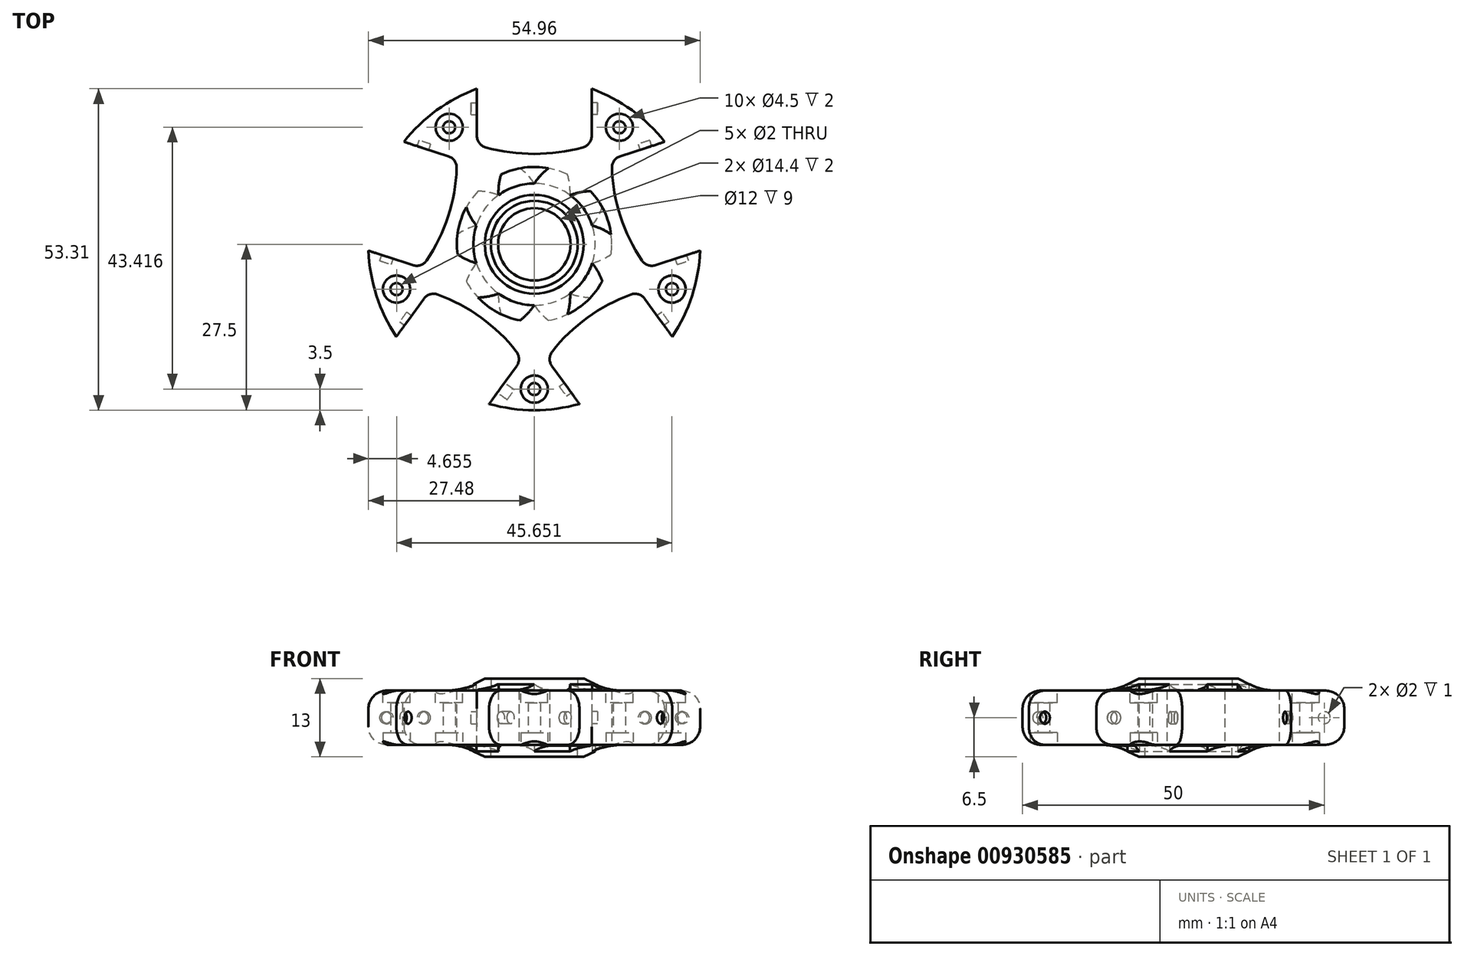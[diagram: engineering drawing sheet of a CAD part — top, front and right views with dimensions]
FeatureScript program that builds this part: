
annotation { "Feature Type Name" : "Feature", "Feature Type Description" : "" }
export const myFeature = defineFeature(function(context is Context, id is Id, definition is map)
    precondition{}
    {
        {
            var Q0;
            Q0=qCreatedBy(makeId("Top.planeOp"),FACE);
            var sketch = newSketch(context, id + "F0", { "sketchPlane" : qUnion([Q0])});
            skCircle(sketch, "E0", {"center": v(0, 0) * mm, "radius": 6 * mm});
            skArc(sketch, "E1", {"start": v(-9.5, 25.8) * mm, "mid": v(-16.16, 22.25) * mm, "end": v(-21.6, 17) * mm});
            skLineSegment(sketch, "E2", {"start": v(0, 0) * mm, "end": v(0, 27.5) * mm, "construction": true});
            skLineSegment(sketch, "E3", {"start": v(0, 0) * mm, "end": v(-26.15, 8.5) * mm, "construction": true});
            skLineSegment(sketch, "E4", {"start": v(0, 0) * mm, "end": v(26.15, 8.5) * mm, "construction": true});
            skLineSegment(sketch, "E5", {"start": v(0, 0) * mm, "end": v(-16.16, -22.25) * mm, "construction": true});
            skLineSegment(sketch, "E6", {"start": v(0, 0) * mm, "end": v(16.16, -22.25) * mm, "construction": true});
            skCircle(sketch, "E7", {"center": v(0, 0) * mm, "radius": 29 * mm, "construction": true});
            skLineSegment(sketch, "E8", {"start": v(-9.5, 25.8) * mm, "end": v(-9.5, 16.51) * mm});
            skLineSegment(sketch, "E9", {"start": v(9.5, 25.8) * mm, "end": v(9.5, 16.51) * mm});
            skCircle(sketch, "E10", {"center": v(0, 0) * mm, "radius": 24 * mm, "construction": true});
            skArc(sketch, "E11", {"start": v(-9.25, 17.51) * mm, "mid": v(0, 16) * mm, "end": v(9.25, 17.51) * mm, "construction": true});
            skLineSegment(sketch, "E12", {"start": v(9.25, 17.51) * mm, "end": v(9.25, 27.49) * mm, "construction": true});
            skLineSegment(sketch, "E13", {"start": v(-9.25, 17.51) * mm, "end": v(-9.25, 27.49) * mm, "construction": true});
            skArc(sketch, "E14", {"start": v(-9.5, 16.51) * mm, "mid": v(0, 15) * mm, "end": v(9.5, 16.51) * mm});
            skLineSegment(sketch, "E15", {"start": v(-21.6, 17) * mm, "end": v(-12.85, 14.16) * mm});
            skLineSegment(sketch, "E16", {"start": v(-27.48, -1.06) * mm, "end": v(-18.72, -3.9) * mm});
            skArc(sketch, "E17", {"start": v(-18.72, -3.9) * mm, "mid": v(-14.27, 4.64) * mm, "end": v(-12.85, 14.16) * mm});
            skArc(sketch, "E18.trimOffspring", {"start": v(-27.48, -1.06) * mm, "mid": v(-26.15, -8.5) * mm, "end": v(-22.85, -15.3) * mm});
            skLineSegment(sketch, "E19", {"start": v(-22.85, -15.3) * mm, "end": v(-17.44, -7.85) * mm});
            skLineSegment(sketch, "E20", {"start": v(-7.48, -26.46) * mm, "end": v(-2.07, -19.01) * mm});
            skArc(sketch, "E21", {"start": v(-2.07, -19.01) * mm, "mid": v(-8.82, -12.14) * mm, "end": v(-17.44, -7.85) * mm});
            skArc(sketch, "E22.trimOffspring", {"start": v(-7.48, -26.46) * mm, "mid": v(0, -27.5) * mm, "end": v(7.48, -26.46) * mm});
            skLineSegment(sketch, "E23", {"start": v(7.48, -26.46) * mm, "end": v(2.07, -19.01) * mm});
            skLineSegment(sketch, "E24", {"start": v(22.85, -15.3) * mm, "end": v(17.44, -7.85) * mm});
            skArc(sketch, "E25", {"start": v(17.44, -7.85) * mm, "mid": v(8.82, -12.14) * mm, "end": v(2.07, -19.01) * mm});
            skArc(sketch, "E26.trimOffspring", {"start": v(22.85, -15.3) * mm, "mid": v(26.15, -8.5) * mm, "end": v(27.48, -1.06) * mm});
            skLineSegment(sketch, "E27", {"start": v(21.6, 17) * mm, "end": v(12.85, 14.16) * mm});
            skLineSegment(sketch, "E28", {"start": v(27.48, -1.06) * mm, "end": v(18.72, -3.9) * mm});
            skArc(sketch, "E29", {"start": v(12.85, 14.16) * mm, "mid": v(14.27, 4.64) * mm, "end": v(18.72, -3.9) * mm});
            skArc(sketch, "E30.trimOffspring", {"start": v(21.6, 17) * mm, "mid": v(16.16, 22.25) * mm, "end": v(9.5, 25.8) * mm});
            skCircle(sketch, "E31", {"center": v(-14.1, 19.42) * mm, "radius": 1 * mm});
            skLineSegment(sketch, "E32", {"start": v(0, 0) * mm, "end": v(-14.1, 19.42) * mm, "construction": true});
            skLineSegment(sketch, "E33", {"start": v(0, 0) * mm, "end": v(14.1, 19.42) * mm, "construction": true});
            skCircle(sketch, "E34", {"center": v(14.1, 19.42) * mm, "radius": 1 * mm});
            skLineSegment(sketch, "E35", {"start": v(-22.83, -7.42) * mm, "end": v(0, 0) * mm, "construction": true});
            skLineSegment(sketch, "E36", {"start": v(0, -24) * mm, "end": v(0, 0) * mm, "construction": true});
            skLineSegment(sketch, "E37", {"start": v(0, 0) * mm, "end": v(22.83, -7.42) * mm, "construction": true});
            skCircle(sketch, "E38", {"center": v(-22.83, -7.42) * mm, "radius": 1 * mm});
            skCircle(sketch, "E39", {"center": v(0, -24) * mm, "radius": 1 * mm});
            skCircle(sketch, "E40", {"center": v(22.83, -7.42) * mm, "radius": 1 * mm});
            skLineSegment(sketch, "E41", {"start": v(-9.5, 22.5) * mm, "end": v(9.5, 22.5) * mm, "construction": true});
            skSolve(sketch);
        }
        {
            var Q0;
            Q0=qSketchRegion(id+"F0",true);
            extrude(context, id + "F1", {"entities" : qUnion([Q0]), "depth" : 9 * mm});
        }
        {
            var Q0;
            Q0=makeQuery(id+"F1.opExtrude","SWEPT_EDGE",EDGE,{"disambiguationData":[OSD([sQuery(id+"F0.wireOp",EDGE,"E8"),sQuery(id+"F0.wireOp",EDGE,"E14")])]});
            var Q1;
            Q1=makeQuery(id+"F1.opExtrude","SWEPT_EDGE",EDGE,{"disambiguationData":[OSD([sQuery(id+"F0.wireOp",EDGE,"E9"),sQuery(id+"F0.wireOp",EDGE,"E14")])]});
            var Q2;
            Q2=makeQuery(id+"F1.opExtrude","SWEPT_EDGE",EDGE,{"disambiguationData":[OSD([sQuery(id+"F0.wireOp",EDGE,"E27"),sQuery(id+"F0.wireOp",EDGE,"E29")])]});
            var Q3;
            Q3=makeQuery(id+"F1.opExtrude","SWEPT_EDGE",EDGE,{"disambiguationData":[OSD([sQuery(id+"F0.wireOp",EDGE,"E28"),sQuery(id+"F0.wireOp",EDGE,"E29")])]});
            var Q4;
            Q4=makeQuery(id+"F1.opExtrude","SWEPT_EDGE",EDGE,{"disambiguationData":[OSD([sQuery(id+"F0.wireOp",EDGE,"E24"),sQuery(id+"F0.wireOp",EDGE,"E25")])]});
            var Q5;
            Q5=makeQuery(id+"F1.opExtrude","SWEPT_EDGE",EDGE,{"disambiguationData":[OSD([sQuery(id+"F0.wireOp",EDGE,"E23"),sQuery(id+"F0.wireOp",EDGE,"E25")])]});
            var Q6;
            Q6=makeQuery(id+"F1.opExtrude","SWEPT_EDGE",EDGE,{"disambiguationData":[OSD([sQuery(id+"F0.wireOp",EDGE,"E20"),sQuery(id+"F0.wireOp",EDGE,"E21")])]});
            var Q7;
            Q7=makeQuery(id+"F1.opExtrude","SWEPT_EDGE",EDGE,{"disambiguationData":[OSD([sQuery(id+"F0.wireOp",EDGE,"E19"),sQuery(id+"F0.wireOp",EDGE,"E21")])]});
            var Q8;
            Q8=makeQuery(id+"F1.opExtrude","SWEPT_EDGE",EDGE,{"disambiguationData":[OSD([sQuery(id+"F0.wireOp",EDGE,"E16"),sQuery(id+"F0.wireOp",EDGE,"E17")])]});
            var Q9;
            Q9=makeQuery(id+"F1.opExtrude","SWEPT_EDGE",EDGE,{"disambiguationData":[OSD([sQuery(id+"F0.wireOp",EDGE,"E15"),sQuery(id+"F0.wireOp",EDGE,"E17")])]});
            fillet(context, id + "F2", {"entities" : qUnion([Q0, Q1, Q2, Q3, Q4, Q5, Q6, Q7, Q8, Q9]), "radius" : 2 * mm, "tangentPropagation" : true, "allowEdgeOverflow" : false});
        }
        {
            var Q0;
            Q0=makeQuery(id+"F1.opExtrude","SWEPT_FACE",FACE,{"disambiguationData":[OSD([sQuery(id+"F0.wireOp",EDGE,"E8")])]});
            var sketch = newSketch(context, id + "F3", { "sketchPlane" : qUnion([Q0])});
            skLineSegment(sketch, "E42", {"start": v(22.5, 9) * mm, "end": v(22.5, 0) * mm, "construction": true});
            skCircle(sketch, "E43", {"center": v(22.5, 4.5) * mm, "radius": 1 * mm});
            skSolve(sketch);
        }
        {
            var Q0;
            Q0=qSketchRegion(id+"F3",true);
            extrude(context, id + "F4", {"entities" : qUnion([Q0]), "operationType" : NewBodyOperationType.REMOVE, "oppositeDirection" : true, "depth" : 1 * mm});
        }
        {
            var Q0;
            Q0=makeQuery(id+"F1.opExtrude","SWEPT_FACE",FACE,{"disambiguationData":[OSD([sQuery(id+"F0.wireOp",EDGE,"E9")])]});
            var sketch = newSketch(context, id + "F5", { "sketchPlane" : qUnion([Q0])});
            skLineSegment(sketch, "E44", {"start": v(-22.5, 0) * mm, "end": v(-22.5, 9) * mm, "construction": true});
            skCircle(sketch, "E45", {"center": v(-22.5, 4.5) * mm, "radius": 1 * mm});
            skSolve(sketch);
        }
        {
            var Q0;
            Q0=qSketchRegion(id+"F5",true);
            extrude(context, id + "F6", {"entities" : qUnion([Q0]), "operationType" : NewBodyOperationType.REMOVE, "oppositeDirection" : true, "depth" : 1 * mm});
        }
        {
            var Q0;
            Q0=makeQuery(id+"F1.opExtrude","SWEPT_FACE",FACE,{"disambiguationData":[OSD([sQuery(id+"F0.wireOp",EDGE,"E15")])]});
            var sketch = newSketch(context, id + "F7", { "sketchPlane" : qUnion([Q0])});
            skLineSegment(sketch, "E46", {"start": v(-22.5, 0) * mm, "end": v(-22.5, 9) * mm, "construction": true});
            skCircle(sketch, "E47", {"center": v(-22.5, 4.5) * mm, "radius": 1 * mm});
            skSolve(sketch);
        }
        {
            var Q0;
            Q0=qSketchRegion(id+"F7",true);
            extrude(context, id + "F8", {"entities" : qUnion([Q0]), "operationType" : NewBodyOperationType.REMOVE, "oppositeDirection" : true, "depth" : 1 * mm});
        }
        {
            var Q0;
            Q0=makeQuery(id+"F1.opExtrude","SWEPT_FACE",FACE,{"disambiguationData":[OSD([sQuery(id+"F0.wireOp",EDGE,"E16")])]});
            var sketch = newSketch(context, id + "F9", { "sketchPlane" : qUnion([Q0])});
            skLineSegment(sketch, "E48", {"start": v(22.5, 9) * mm, "end": v(22.5, 0) * mm, "construction": true});
            skCircle(sketch, "E49", {"center": v(22.5, 4.5) * mm, "radius": 1 * mm});
            skSolve(sketch);
        }
        {
            var Q0;
            Q0=qSketchRegion(id+"F9",true);
            extrude(context, id + "F10", {"entities" : qUnion([Q0]), "operationType" : NewBodyOperationType.REMOVE, "oppositeDirection" : true, "depth" : 1 * mm});
        }
        {
            var Q0;
            Q0=makeQuery(id+"F1.opExtrude","SWEPT_FACE",FACE,{"disambiguationData":[OSD([sQuery(id+"F0.wireOp",EDGE,"E19")])]});
            var sketch = newSketch(context, id + "F11", { "sketchPlane" : qUnion([Q0])});
            skLineSegment(sketch, "E50", {"start": v(-22.5, 0) * mm, "end": v(-22.5, 9) * mm, "construction": true});
            skCircle(sketch, "E51", {"center": v(-22.5, 4.5) * mm, "radius": 1 * mm});
            skSolve(sketch);
        }
        {
            var Q0;
            Q0=qSketchRegion(id+"F11",true);
            extrude(context, id + "F12", {"entities" : qUnion([Q0]), "operationType" : NewBodyOperationType.REMOVE, "oppositeDirection" : true, "depth" : 1 * mm});
        }
        {
            var Q0;
            Q0=makeQuery(id+"F1.opExtrude","SWEPT_FACE",FACE,{"disambiguationData":[OSD([sQuery(id+"F0.wireOp",EDGE,"E20")])]});
            var sketch = newSketch(context, id + "F13", { "sketchPlane" : qUnion([Q0])});
            skLineSegment(sketch, "E52", {"start": v(22.5, 9) * mm, "end": v(22.5, 0) * mm, "construction": true});
            skCircle(sketch, "E53", {"center": v(22.5, 4.5) * mm, "radius": 1 * mm});
            skSolve(sketch);
        }
        {
            var Q0;
            Q0=qSketchRegion(id+"F13",true);
            extrude(context, id + "F14", {"entities" : qUnion([Q0]), "operationType" : NewBodyOperationType.REMOVE, "oppositeDirection" : true, "depth" : 2 * mm});
        }
        {
            var Q0;
            Q0=makeQuery(id+"F1.opExtrude","SWEPT_FACE",FACE,{"disambiguationData":[OSD([sQuery(id+"F0.wireOp",EDGE,"E23")])]});
            var sketch = newSketch(context, id + "F15", { "sketchPlane" : qUnion([Q0])});
            skLineSegment(sketch, "E54", {"start": v(-22.5, 0) * mm, "end": v(-22.5, 9) * mm, "construction": true});
            skCircle(sketch, "E55", {"center": v(-22.5, 4.5) * mm, "radius": 1 * mm});
            skSolve(sketch);
        }
        {
            var Q0;
            Q0=qSketchRegion(id+"F15",true);
            extrude(context, id + "F16", {"entities" : qUnion([Q0]), "operationType" : NewBodyOperationType.REMOVE, "oppositeDirection" : true, "depth" : 1 * mm});
        }
        {
            var Q0;
            Q0=makeQuery(id+"F1.opExtrude","SWEPT_FACE",FACE,{"disambiguationData":[OSD([sQuery(id+"F0.wireOp",EDGE,"E24")])]});
            var sketch = newSketch(context, id + "F17", { "sketchPlane" : qUnion([Q0])});
            skLineSegment(sketch, "E56", {"start": v(22.5, 9) * mm, "end": v(22.5, 0) * mm, "construction": true});
            skCircle(sketch, "E57", {"center": v(22.5, 4.5) * mm, "radius": 1 * mm});
            skSolve(sketch);
        }
        {
            var Q0;
            Q0=qSketchRegion(id+"F17",true);
            extrude(context, id + "F18", {"entities" : qUnion([Q0]), "operationType" : NewBodyOperationType.REMOVE, "oppositeDirection" : true, "depth" : 1 * mm});
        }
        {
            var Q0;
            Q0=makeQuery(id+"F1.opExtrude","SWEPT_FACE",FACE,{"disambiguationData":[OSD([sQuery(id+"F0.wireOp",EDGE,"E28")])]});
            var sketch = newSketch(context, id + "F19", { "sketchPlane" : qUnion([Q0])});
            skLineSegment(sketch, "E58", {"start": v(-22.5, 0) * mm, "end": v(-22.5, 9) * mm, "construction": true});
            skCircle(sketch, "E59", {"center": v(-22.5, 4.5) * mm, "radius": 1 * mm});
            skSolve(sketch);
        }
        {
            var Q0;
            Q0=qSketchRegion(id+"F19",true);
            extrude(context, id + "F20", {"entities" : qUnion([Q0]), "operationType" : NewBodyOperationType.REMOVE, "oppositeDirection" : true, "depth" : 1 * mm});
        }
        {
            var Q0;
            Q0=makeQuery(id+"F1.opExtrude","SWEPT_FACE",FACE,{"disambiguationData":[OSD([sQuery(id+"F0.wireOp",EDGE,"E27")])]});
            var sketch = newSketch(context, id + "F21", { "sketchPlane" : qUnion([Q0])});
            skLineSegment(sketch, "E60", {"start": v(22.5, 9) * mm, "end": v(22.5, 0) * mm, "construction": true});
            skCircle(sketch, "E61", {"center": v(22.5, 4.5) * mm, "radius": 1 * mm});
            skSolve(sketch);
        }
        {
            var Q0;
            Q0=qSketchRegion(id+"F21",true);
            extrude(context, id + "F22", {"entities" : qUnion([Q0]), "operationType" : NewBodyOperationType.REMOVE, "oppositeDirection" : true, "depth" : 1 * mm});
        }
        {
            var Q0;
            Q0=makeQuery(id+"F1.opExtrude","CAP_FACE",FACE,{"disambiguationData":[OSD([sQuery(id+"F0.wireOp",EDGE,"E0"),sQuery(id+"F0.wireOp",EDGE,"E1"),sQuery(id+"F0.wireOp",EDGE,"E8"),sQuery(id+"F0.wireOp",EDGE,"E9"),sQuery(id+"F0.wireOp",EDGE,"E14"),sQuery(id+"F0.wireOp",EDGE,"E15"),sQuery(id+"F0.wireOp",EDGE,"E16"),sQuery(id+"F0.wireOp",EDGE,"E17"),sQuery(id+"F0.wireOp",EDGE,"E18.trimOffspring"),sQuery(id+"F0.wireOp",EDGE,"E19"),sQuery(id+"F0.wireOp",EDGE,"E20"),sQuery(id+"F0.wireOp",EDGE,"E21"),sQuery(id+"F0.wireOp",EDGE,"E22.trimOffspring"),sQuery(id+"F0.wireOp",EDGE,"E23"),sQuery(id+"F0.wireOp",EDGE,"E24"),sQuery(id+"F0.wireOp",EDGE,"E25"),sQuery(id+"F0.wireOp",EDGE,"E26.trimOffspring"),sQuery(id+"F0.wireOp",EDGE,"E27"),sQuery(id+"F0.wireOp",EDGE,"E28"),sQuery(id+"F0.wireOp",EDGE,"E29"),sQuery(id+"F0.wireOp",EDGE,"E30.trimOffspring"),sQuery(id+"F0.wireOp",EDGE,"E31"),sQuery(id+"F0.wireOp",EDGE,"E34"),sQuery(id+"F0.wireOp",EDGE,"E38"),sQuery(id+"F0.wireOp",EDGE,"E39"),sQuery(id+"F0.wireOp",EDGE,"E40")])],"isStart":false});
            var sketch = newSketch(context, id + "F23", { "sketchPlane" : qUnion([Q0])});
            skCircle(sketch, "E62", {"center": v(0, 0) * mm, "radius": 7.2 * mm});
            skCircle(sketch, "E63", {"center": v(0, 0) * mm, "radius": 12.2 * mm});
            skSolve(sketch);
        }
        {
            var Q0;
            Q0=qSketchRegion(id+"F23",true);
            extrude(context, id + "F24", {"entities" : qUnion([Q0]), "operationType" : NewBodyOperationType.ADD, "depth" : 2 * mm});
        }
        {
            var Q0;
            Q0=makeQuery(id+"F1.opExtrude","CAP_EDGE",EDGE,{"disambiguationData":[OSD([sQuery(id+"F0.wireOp",EDGE,"E18.trimOffspring")])],"isStart":false});
            var Q1;
            Q1=makeQuery(id+"F1.opExtrude","CAP_EDGE",EDGE,{"disambiguationData":[OSD([sQuery(id+"F0.wireOp",EDGE,"E18.trimOffspring")])],"isStart":true});
            var Q2;
            Q2=makeQuery(id+"F1.opExtrude","CAP_EDGE",EDGE,{"disambiguationData":[OSD([sQuery(id+"F0.wireOp",EDGE,"E22.trimOffspring")])],"isStart":false});
            var Q3;
            Q3=makeQuery(id+"F1.opExtrude","CAP_EDGE",EDGE,{"disambiguationData":[OSD([sQuery(id+"F0.wireOp",EDGE,"E22.trimOffspring")])],"isStart":true});
            var Q4;
            Q4=makeQuery(id+"F1.opExtrude","CAP_EDGE",EDGE,{"disambiguationData":[OSD([sQuery(id+"F0.wireOp",EDGE,"E26.trimOffspring")])],"isStart":true});
            var Q5;
            Q5=makeQuery(id+"F1.opExtrude","CAP_EDGE",EDGE,{"disambiguationData":[OSD([sQuery(id+"F0.wireOp",EDGE,"E26.trimOffspring")])],"isStart":false});
            var Q6;
            Q6=makeQuery(id+"F1.opExtrude","CAP_EDGE",EDGE,{"disambiguationData":[OSD([sQuery(id+"F0.wireOp",EDGE,"E30.trimOffspring")])],"isStart":true});
            var Q7;
            Q7=makeQuery(id+"F1.opExtrude","CAP_EDGE",EDGE,{"disambiguationData":[OSD([sQuery(id+"F0.wireOp",EDGE,"E30.trimOffspring")])],"isStart":false});
            var Q8;
            Q8=makeQuery(id+"F1.opExtrude","CAP_EDGE",EDGE,{"disambiguationData":[OSD([sQuery(id+"F0.wireOp",EDGE,"E1")])],"isStart":true});
            var Q9;
            Q9=makeQuery(id+"F1.opExtrude","CAP_EDGE",EDGE,{"disambiguationData":[OSD([sQuery(id+"F0.wireOp",EDGE,"E1")])],"isStart":false});
            fillet(context, id + "F25", {"entities" : qUnion([Q0, Q1, Q2, Q3, Q4, Q5, Q6, Q7, Q8, Q9]), "radius" : 3 * mm, "tangentPropagation" : true, "allowEdgeOverflow" : false});
        }
        {
            var Q0;
            {var subQ0=sQuery(id+"F0.wireOp",EDGE,"E34");var subQ1=sQuery(id+"F0.wireOp",EDGE,"E31");var subQ2=sQuery(id+"F0.wireOp",EDGE,"E30.trimOffspring");var subQ3=sQuery(id+"F0.wireOp",EDGE,"E29");var subQ4=sQuery(id+"F0.wireOp",EDGE,"E28");var subQ5=sQuery(id+"F0.wireOp",EDGE,"E27");var subQ6=sQuery(id+"F0.wireOp",EDGE,"E26.trimOffspring");var subQ7=sQuery(id+"F0.wireOp",EDGE,"E25");var subQ8=sQuery(id+"F0.wireOp",EDGE,"E24");var subQ9=sQuery(id+"F0.wireOp",EDGE,"E23");var subQ10=sQuery(id+"F0.wireOp",EDGE,"E22.trimOffspring");var subQ11=sQuery(id+"F0.wireOp",EDGE,"E21");var subQ12=sQuery(id+"F0.wireOp",EDGE,"E14");var subQ13=sQuery(id+"F0.wireOp",EDGE,"E9");var subQ14=sQuery(id+"F0.wireOp",EDGE,"E8");var subQ15=sQuery(id+"F0.wireOp",EDGE,"E1");var subQ16=sQuery(id+"F0.wireOp",EDGE,"E15");var subQ17=sQuery(id+"F0.wireOp",EDGE,"E16");var subQ18=sQuery(id+"F0.wireOp",EDGE,"E17");var subQ19=sQuery(id+"F0.wireOp",EDGE,"E18.trimOffspring");var subQ20=sQuery(id+"F0.wireOp",EDGE,"E19");var subQ21=sQuery(id+"F0.wireOp",EDGE,"E20");var subQ22=sQuery(id+"F0.wireOp",EDGE,"E38");var subQ23=sQuery(id+"F0.wireOp",EDGE,"E39");var subQ24=sQuery(id+"F0.wireOp",EDGE,"E40");Q0=makeQuery(id+"F24.boolean.opBoolean","SPLIT",FACE,{"disambiguationData":[TD([makeQuery(id+"F1.opExtrude","SWEPT_FACE",FACE,{"disambiguationData":[OSD([subQ15])]})])],"derivedFrom":makeQuery(id+"F1.opExtrude","CAP_FACE",FACE,{"disambiguationData":[OSD([sQuery(id+"F0.wireOp",EDGE,"E0"),subQ15,subQ14,subQ13,subQ12,subQ16,subQ17,subQ18,subQ19,subQ20,subQ21,subQ11,subQ10,subQ9,subQ8,subQ7,subQ6,subQ5,subQ4,subQ3,subQ2,subQ1,subQ0,subQ22,subQ23,subQ24])],"isStart":false})});}
            var sketch = newSketch(context, id + "F26", { "sketchPlane" : qUnion([Q0])});
            skCircle(sketch, "E64", {"center": v(-14.1, 19.42) * mm, "radius": 2.25 * mm});
            skCircle(sketch, "E65", {"center": v(14.1, 19.42) * mm, "radius": 2.25 * mm});
            skCircle(sketch, "E66", {"center": v(22.83, -7.42) * mm, "radius": 2.25 * mm});
            skCircle(sketch, "E67", {"center": v(0, -24) * mm, "radius": 2.25 * mm});
            skCircle(sketch, "E68", {"center": v(-22.83, -7.42) * mm, "radius": 2.25 * mm});
            skSolve(sketch);
        }
        {
            var Q0;
            Q0=qSketchRegion(id+"F26",true);
            extrude(context, id + "F27", {"entities" : qUnion([Q0]), "operationType" : NewBodyOperationType.REMOVE, "oppositeDirection" : true, "depth" : 2 * mm});
        }
        {
            var Q0;
            Q0=makeQuery(id+"F1.opExtrude","CAP_FACE",FACE,{"disambiguationData":[OSD([sQuery(id+"F0.wireOp",EDGE,"E0"),sQuery(id+"F0.wireOp",EDGE,"E1"),sQuery(id+"F0.wireOp",EDGE,"E8"),sQuery(id+"F0.wireOp",EDGE,"E9"),sQuery(id+"F0.wireOp",EDGE,"E14"),sQuery(id+"F0.wireOp",EDGE,"E15"),sQuery(id+"F0.wireOp",EDGE,"E16"),sQuery(id+"F0.wireOp",EDGE,"E17"),sQuery(id+"F0.wireOp",EDGE,"E18.trimOffspring"),sQuery(id+"F0.wireOp",EDGE,"E19"),sQuery(id+"F0.wireOp",EDGE,"E20"),sQuery(id+"F0.wireOp",EDGE,"E21"),sQuery(id+"F0.wireOp",EDGE,"E22.trimOffspring"),sQuery(id+"F0.wireOp",EDGE,"E23"),sQuery(id+"F0.wireOp",EDGE,"E24"),sQuery(id+"F0.wireOp",EDGE,"E25"),sQuery(id+"F0.wireOp",EDGE,"E26.trimOffspring"),sQuery(id+"F0.wireOp",EDGE,"E27"),sQuery(id+"F0.wireOp",EDGE,"E28"),sQuery(id+"F0.wireOp",EDGE,"E29"),sQuery(id+"F0.wireOp",EDGE,"E30.trimOffspring"),sQuery(id+"F0.wireOp",EDGE,"E31"),sQuery(id+"F0.wireOp",EDGE,"E34"),sQuery(id+"F0.wireOp",EDGE,"E38"),sQuery(id+"F0.wireOp",EDGE,"E39"),sQuery(id+"F0.wireOp",EDGE,"E40")])],"isStart":true});
            var sketch = newSketch(context, id + "F28", { "sketchPlane" : qUnion([Q0])});
            skCircle(sketch, "E69", {"center": v(-22.83, 7.42) * mm, "radius": 2.25 * mm});
            skCircle(sketch, "E70", {"center": v(0, 24) * mm, "radius": 2.25 * mm});
            skCircle(sketch, "E71", {"center": v(22.83, 7.42) * mm, "radius": 2.25 * mm});
            skCircle(sketch, "E72", {"center": v(14.1, -19.42) * mm, "radius": 2.25 * mm});
            skCircle(sketch, "E73", {"center": v(-14.1, -19.42) * mm, "radius": 2.25 * mm});
            skSolve(sketch);
        }
        {
            var Q0;
            Q0=qSketchRegion(id+"F28",true);
            extrude(context, id + "F29", {"entities" : qUnion([Q0]), "operationType" : NewBodyOperationType.REMOVE, "oppositeDirection" : true, "depth" : 2 * mm});
        }
        {
            var Q0;
            Q0=makeQuery(id+"F1.opExtrude","CAP_FACE",FACE,{"disambiguationData":[OSD([sQuery(id+"F0.wireOp",EDGE,"E0"),sQuery(id+"F0.wireOp",EDGE,"E1"),sQuery(id+"F0.wireOp",EDGE,"E8"),sQuery(id+"F0.wireOp",EDGE,"E9"),sQuery(id+"F0.wireOp",EDGE,"E14"),sQuery(id+"F0.wireOp",EDGE,"E15"),sQuery(id+"F0.wireOp",EDGE,"E16"),sQuery(id+"F0.wireOp",EDGE,"E17"),sQuery(id+"F0.wireOp",EDGE,"E18.trimOffspring"),sQuery(id+"F0.wireOp",EDGE,"E19"),sQuery(id+"F0.wireOp",EDGE,"E20"),sQuery(id+"F0.wireOp",EDGE,"E21"),sQuery(id+"F0.wireOp",EDGE,"E22.trimOffspring"),sQuery(id+"F0.wireOp",EDGE,"E23"),sQuery(id+"F0.wireOp",EDGE,"E24"),sQuery(id+"F0.wireOp",EDGE,"E25"),sQuery(id+"F0.wireOp",EDGE,"E26.trimOffspring"),sQuery(id+"F0.wireOp",EDGE,"E27"),sQuery(id+"F0.wireOp",EDGE,"E28"),sQuery(id+"F0.wireOp",EDGE,"E29"),sQuery(id+"F0.wireOp",EDGE,"E30.trimOffspring"),sQuery(id+"F0.wireOp",EDGE,"E31"),sQuery(id+"F0.wireOp",EDGE,"E34"),sQuery(id+"F0.wireOp",EDGE,"E38"),sQuery(id+"F0.wireOp",EDGE,"E39"),sQuery(id+"F0.wireOp",EDGE,"E40")])],"isStart":true});
            var sketch = newSketch(context, id + "F30", { "sketchPlane" : qUnion([Q0])});
            skCircle(sketch, "E74", {"center": v(0, 0) * mm, "radius": 7.2 * mm});
            skCircle(sketch, "E75", {"center": v(0, 0) * mm, "radius": 12.2 * mm});
            skSolve(sketch);
        }
        {
            var Q0;
            Q0=qSketchRegion(id+"F30",true);
            extrude(context, id + "F31", {"entities" : qUnion([Q0]), "operationType" : NewBodyOperationType.ADD, "depth" : 2 * mm});
        }
        {
            var Q0;
            Q0=makeQuery(id+"F24.opExtrude","CAP_EDGE",EDGE,{"disambiguationData":[OSD([sQuery(id+"F23.wireOp",EDGE,"E63")])],"isStart":false});
            var Q1;
            Q1=makeQuery(id+"F31.opExtrude","CAP_EDGE",EDGE,{"disambiguationData":[OSD([sQuery(id+"F30.wireOp",EDGE,"E75")])],"isStart":false});
            chamfer(context, id + "F32", {"entities" : qUnion([Q0, Q1]), "chamferType" : ChamferType.TWO_OFFSETS, "width1" : 4 * mm, "oppositeDirection" : false, "width2" : 2 * mm, "tangentPropagation" : true});
        }
        {
            var Q0;
            {var subQ0=sQuery(id+"F0.wireOp",EDGE,"E34");var subQ1=sQuery(id+"F0.wireOp",EDGE,"E31");var subQ2=sQuery(id+"F0.wireOp",EDGE,"E30.trimOffspring");var subQ3=sQuery(id+"F23.wireOp",EDGE,"E63");var subQ4=sQuery(id+"F0.wireOp",EDGE,"E29");var subQ5=sQuery(id+"F0.wireOp",EDGE,"E28");var subQ6=sQuery(id+"F0.wireOp",EDGE,"E27");var subQ7=sQuery(id+"F0.wireOp",EDGE,"E26.trimOffspring");var subQ8=sQuery(id+"F0.wireOp",EDGE,"E25");var subQ9=sQuery(id+"F0.wireOp",EDGE,"E24");var subQ10=sQuery(id+"F0.wireOp",EDGE,"E23");var subQ11=sQuery(id+"F0.wireOp",EDGE,"E22.trimOffspring");var subQ12=sQuery(id+"F0.wireOp",EDGE,"E21");var subQ13=sQuery(id+"F0.wireOp",EDGE,"E14");var subQ14=sQuery(id+"F0.wireOp",EDGE,"E9");var subQ15=sQuery(id+"F0.wireOp",EDGE,"E8");var subQ16=sQuery(id+"F0.wireOp",EDGE,"E1");var subQ17=sQuery(id+"F0.wireOp",EDGE,"E15");var subQ18=sQuery(id+"F0.wireOp",EDGE,"E16");var subQ19=sQuery(id+"F0.wireOp",EDGE,"E17");var subQ20=sQuery(id+"F0.wireOp",EDGE,"E18.trimOffspring");var subQ21=sQuery(id+"F0.wireOp",EDGE,"E19");var subQ22=sQuery(id+"F0.wireOp",EDGE,"E20");var subQ23=sQuery(id+"F0.wireOp",EDGE,"E38");var subQ24=sQuery(id+"F0.wireOp",EDGE,"E39");var subQ25=sQuery(id+"F0.wireOp",EDGE,"E40");Q0=makeQuery(id+"F32.opChamfer","BLEND_EDGE",EDGE,{"blendedFrom":[makeQuery(id+"F24.opExtrude","CAP_EDGE",EDGE,{"disambiguationData":[OSD([subQ3])],"isStart":false}),makeQuery(id+"F24.boolean.opBoolean","SPLIT",FACE,{"disambiguationData":[TD([makeQuery(id+"F1.opExtrude","SWEPT_FACE",FACE,{"disambiguationData":[OSD([subQ16])]})])],"derivedFrom":makeQuery(id+"F1.opExtrude","CAP_FACE",FACE,{"disambiguationData":[OSD([sQuery(id+"F0.wireOp",EDGE,"E0"),subQ16,subQ15,subQ14,subQ13,subQ17,subQ18,subQ19,subQ20,subQ21,subQ22,subQ12,subQ11,subQ10,subQ9,subQ8,subQ7,subQ6,subQ5,subQ4,subQ2,subQ1,subQ0,subQ23,subQ24,subQ25])],"isStart":false})})],"blendedInto":[makeQuery(id+"F24.boolean.opBoolean","SPLIT",FACE,{"disambiguationData":[TD([makeQuery(id+"F1.opExtrude","SWEPT_FACE",FACE,{"disambiguationData":[OSD([subQ16])]})])],"derivedFrom":makeQuery(id+"F1.opExtrude","CAP_FACE",FACE,{"disambiguationData":[OSD([sQuery(id+"F0.wireOp",EDGE,"E0"),subQ16,subQ15,subQ14,subQ13,subQ17,subQ18,subQ19,subQ20,subQ21,subQ22,subQ12,subQ11,subQ10,subQ9,subQ8,subQ7,subQ6,subQ5,subQ4,subQ2,subQ1,subQ0,subQ23,subQ24,subQ25])],"isStart":false})})]});}
            var Q1;
            {var subQ0=sQuery(id+"F0.wireOp",EDGE,"E21");var subQ1=sQuery(id+"F0.wireOp",EDGE,"E20");var subQ2=sQuery(id+"F0.wireOp",EDGE,"E30.trimOffspring");var subQ3=sQuery(id+"F0.wireOp",EDGE,"E14");var subQ4=sQuery(id+"F0.wireOp",EDGE,"E9");var subQ5=sQuery(id+"F0.wireOp",EDGE,"E22.trimOffspring");var subQ6=sQuery(id+"F0.wireOp",EDGE,"E29");var subQ7=sQuery(id+"F0.wireOp",EDGE,"E28");var subQ8=sQuery(id+"F0.wireOp",EDGE,"E27");var subQ9=sQuery(id+"F0.wireOp",EDGE,"E25");var subQ10=sQuery(id+"F0.wireOp",EDGE,"E24");var subQ11=sQuery(id+"F0.wireOp",EDGE,"E15");var subQ12=sQuery(id+"F0.wireOp",EDGE,"E8");var subQ13=sQuery(id+"F0.wireOp",EDGE,"E23");var subQ14=sQuery(id+"F0.wireOp",EDGE,"E16");var subQ15=sQuery(id+"F0.wireOp",EDGE,"E17");var subQ16=sQuery(id+"F0.wireOp",EDGE,"E19");var subQ17=sQuery(id+"F0.wireOp",EDGE,"E26.trimOffspring");var subQ18=sQuery(id+"F0.wireOp",EDGE,"E1");var subQ19=sQuery(id+"F0.wireOp",EDGE,"E18.trimOffspring");var subQ20=sQuery(id+"F30.wireOp",EDGE,"E75");Q1=makeQuery(id+"F32.opChamfer","BLEND_EDGE",EDGE,{"blendedFrom":[makeQuery(id+"F31.opExtrude","CAP_EDGE",EDGE,{"disambiguationData":[OSD([subQ20])],"isStart":false}),makeQuery(id+"F31.boolean.opBoolean","SPLIT",FACE,{"disambiguationData":[TD([makeQuery(id+"F1.opExtrude","SWEPT_FACE",FACE,{"disambiguationData":[OSD([subQ12])]})])],"derivedFrom":makeQuery(id+"F1.opExtrude","CAP_FACE",FACE,{"disambiguationData":[OSD([sQuery(id+"F0.wireOp",EDGE,"E0"),subQ18,subQ12,subQ4,subQ3,subQ11,subQ14,subQ15,subQ19,subQ16,subQ1,subQ0,subQ5,subQ13,subQ10,subQ9,subQ17,subQ8,subQ7,subQ6,subQ2,sQuery(id+"F0.wireOp",EDGE,"E31"),sQuery(id+"F0.wireOp",EDGE,"E34"),sQuery(id+"F0.wireOp",EDGE,"E38"),sQuery(id+"F0.wireOp",EDGE,"E39"),sQuery(id+"F0.wireOp",EDGE,"E40")])],"isStart":true})})],"blendedInto":[makeQuery(id+"F31.boolean.opBoolean","SPLIT",FACE,{"disambiguationData":[TD([makeQuery(id+"F1.opExtrude","SWEPT_FACE",FACE,{"disambiguationData":[OSD([subQ12])]})])],"derivedFrom":makeQuery(id+"F1.opExtrude","CAP_FACE",FACE,{"disambiguationData":[OSD([sQuery(id+"F0.wireOp",EDGE,"E0"),subQ18,subQ12,subQ4,subQ3,subQ11,subQ14,subQ15,subQ19,subQ16,subQ1,subQ0,subQ5,subQ13,subQ10,subQ9,subQ17,subQ8,subQ7,subQ6,subQ2,sQuery(id+"F0.wireOp",EDGE,"E31"),sQuery(id+"F0.wireOp",EDGE,"E34"),sQuery(id+"F0.wireOp",EDGE,"E38"),sQuery(id+"F0.wireOp",EDGE,"E39"),sQuery(id+"F0.wireOp",EDGE,"E40")])],"isStart":true})})]});}
            fillet(context, id + "F33", {"entities" : qUnion([Q0, Q1]), "radius" : 10 * mm, "tangentPropagation" : true, "allowEdgeOverflow" : false});
        }
        {
            var Q0;
            Q0=makeQuery(id+"F24.opExtrude","CAP_FACE",FACE,{"disambiguationData":[OSD([sQuery(id+"F23.wireOp",EDGE,"E62"),sQuery(id+"F23.wireOp",EDGE,"E63")])],"isStart":false});
            var sketch = newSketch(context, id + "F34", { "sketchPlane" : qUnion([Q0])});
            skLineSegment(sketch, "E76", {"start": v(0, 0) * mm, "end": v(0, 14.56) * mm, "construction": true});
            skLineSegment(sketch, "E77", {"start": v(0, 0) * mm, "end": v(-13.85, 4.5) * mm, "construction": true});
            skLineSegment(sketch, "E78", {"start": v(0, 0) * mm, "end": v(-8.56, -11.78) * mm, "construction": true});
            skLineSegment(sketch, "E79", {"start": v(0, 0) * mm, "end": v(13.85, 4.5) * mm, "construction": true});
            skLineSegment(sketch, "E80", {"start": v(0, 0) * mm, "end": v(8.56, -11.78) * mm, "construction": true});
            skArc(sketch, "E81", {"start": v(0, 10.09) * mm, "mid": v(-3.12, 9.6) * mm, "end": v(-5.93, 8.16) * mm});
            skArc(sketch, "E82", {"start": v(4.5, 13.85) * mm, "mid": v(0, 14.56) * mm, "end": v(-4.5, 13.85) * mm});
            skLineSegment(sketch, "E83", {"start": v(-5.93, 8.16) * mm, "end": v(0, 0) * mm, "construction": true});
            skLineSegment(sketch, "E84", {"start": v(4.5, 13.85) * mm, "end": v(0, 0) * mm, "construction": true});
            skLineSegment(sketch, "E85", {"start": v(-4.5, 13.85) * mm, "end": v(0, 0) * mm, "construction": true});
            skArc(sketch, "E86", {"start": v(-4.5, 13.85) * mm, "mid": v(-5.64, 11.11) * mm, "end": v(-5.93, 8.16) * mm});
            skArc(sketch, "E87", {"start": v(4.5, 13.85) * mm, "mid": v(1.97, 12.3) * mm, "end": v(0, 10.09) * mm});
            skLineSegment(sketch, "E88", {"start": v(0, 0) * mm, "end": v(5.93, 8.16) * mm, "construction": true});
            skLineSegment(sketch, "E89", {"start": v(0, 0) * mm, "end": v(11.78, 8.56) * mm, "construction": true});
            skLineSegment(sketch, "E90", {"start": v(0, 0) * mm, "end": v(14.56, 0) * mm, "construction": true});
            skArc(sketch, "E91", {"start": v(9.6, 3.12) * mm, "mid": v(8.16, 5.93) * mm, "end": v(5.93, 8.16) * mm});
            skArc(sketch, "E92", {"start": v(14.56, 0) * mm, "mid": v(13.85, 4.5) * mm, "end": v(11.78, 8.56) * mm});
            skArc(sketch, "E93", {"start": v(11.78, 8.56) * mm, "mid": v(8.83, 8.8) * mm, "end": v(5.93, 8.16) * mm});
            skArc(sketch, "E94", {"start": v(14.56, 0) * mm, "mid": v(12.31, 1.93) * mm, "end": v(9.6, 3.12) * mm});
            skLineSegment(sketch, "E95", {"start": v(0, 0) * mm, "end": v(9.6, -3.12) * mm, "construction": true});
            skLineSegment(sketch, "E96", {"start": v(0, 0) * mm, "end": v(11.78, -8.56) * mm, "construction": true});
            skLineSegment(sketch, "E97", {"start": v(0, 0) * mm, "end": v(4.5, -13.85) * mm, "construction": true});
            skArc(sketch, "E98", {"start": v(5.93, -8.16) * mm, "mid": v(8.16, -5.93) * mm, "end": v(9.6, -3.12) * mm});
            skArc(sketch, "E99", {"start": v(4.5, -13.85) * mm, "mid": v(8.56, -11.78) * mm, "end": v(11.78, -8.56) * mm});
            skArc(sketch, "E100", {"start": v(11.78, -8.56) * mm, "mid": v(11.1, -5.67) * mm, "end": v(9.6, -3.12) * mm});
            skArc(sketch, "E101", {"start": v(4.5, -13.85) * mm, "mid": v(5.64, -11.11) * mm, "end": v(5.93, -8.16) * mm});
            skLineSegment(sketch, "E102", {"start": v(0, 0) * mm, "end": v(0, -10.09) * mm, "construction": true});
            skLineSegment(sketch, "E103", {"start": v(0, 0) * mm, "end": v(-4.5, -13.85) * mm, "construction": true});
            skLineSegment(sketch, "E104", {"start": v(0, 0) * mm, "end": v(-11.78, -8.56) * mm, "construction": true});
            skArc(sketch, "E105", {"start": v(-5.93, -8.16) * mm, "mid": v(-3.12, -9.6) * mm, "end": v(0, -10.09) * mm});
            skArc(sketch, "E106", {"start": v(-11.78, -8.56) * mm, "mid": v(-8.56, -11.78) * mm, "end": v(-4.5, -13.85) * mm});
            skArc(sketch, "E107", {"start": v(-11.78, -8.56) * mm, "mid": v(-8.83, -8.8) * mm, "end": v(-5.93, -8.16) * mm});
            skArc(sketch, "E108", {"start": v(-4.5, -13.85) * mm, "mid": v(-1.97, -12.3) * mm, "end": v(0, -10.09) * mm});
            skLineSegment(sketch, "E109", {"start": v(0, 0) * mm, "end": v(-9.6, -3.12) * mm, "construction": true});
            skLineSegment(sketch, "E110", {"start": v(0, 0) * mm, "end": v(-14.56, 0) * mm, "construction": true});
            skLineSegment(sketch, "E111", {"start": v(0, 0) * mm, "end": v(-11.78, 8.56) * mm, "construction": true});
            skArc(sketch, "E112", {"start": v(-9.6, 3.12) * mm, "mid": v(-10.09, 0) * mm, "end": v(-9.6, -3.12) * mm});
            skArc(sketch, "E113", {"start": v(-11.78, 8.56) * mm, "mid": v(-13.85, 4.5) * mm, "end": v(-14.56, 0) * mm});
            skArc(sketch, "E114", {"start": v(-11.78, 8.56) * mm, "mid": v(-11.1, 5.67) * mm, "end": v(-9.6, 3.12) * mm});
            skArc(sketch, "E115", {"start": v(-14.56, 0) * mm, "mid": v(-12.31, -1.93) * mm, "end": v(-9.6, -3.12) * mm});
            skSolve(sketch);
        }
        {
            var Q0;
            Q0=qSketchRegion(id+"F34",true);
            extrude(context, id + "F35", {"entities" : qUnion([Q0]), "operationType" : NewBodyOperationType.REMOVE, "oppositeDirection" : true, "depth" : 1.85 * mm});
        }
        {
            var Q0;
            Q0=makeQuery(id+"F31.opExtrude","CAP_FACE",FACE,{"disambiguationData":[OSD([sQuery(id+"F30.wireOp",EDGE,"E74"),sQuery(id+"F30.wireOp",EDGE,"E75")])],"isStart":false});
            var sketch = newSketch(context, id + "F36", { "sketchPlane" : qUnion([Q0])});
            skLineSegment(sketch, "E116", {"start": v(0, 14.56) * mm, "end": v(0, -14.56) * mm, "construction": true});
            skLineSegment(sketch, "E117", {"start": v(-14.56, 0) * mm, "end": v(14.56, 0) * mm, "construction": true});
            skLineSegment(sketch, "E118", {"start": v(0, 0) * mm, "end": v(-4.5, 13.85) * mm, "construction": true});
            skLineSegment(sketch, "E119", {"start": v(0, 0) * mm, "end": v(4.5, -13.85) * mm, "construction": true});
            skLineSegment(sketch, "E120", {"start": v(-8.56, 11.78) * mm, "end": v(8.56, -11.78) * mm, "construction": true});
            skLineSegment(sketch, "E121", {"start": v(-11.78, 8.56) * mm, "end": v(11.78, -8.56) * mm, "construction": true});
            skLineSegment(sketch, "E122", {"start": v(-13.85, 4.5) * mm, "end": v(13.85, -4.5) * mm, "construction": true});
            skLineSegment(sketch, "E123", {"start": v(-13.85, -4.5) * mm, "end": v(13.85, 4.5) * mm, "construction": true});
            skLineSegment(sketch, "E124", {"start": v(-11.78, -8.56) * mm, "end": v(11.78, 8.56) * mm, "construction": true});
            skLineSegment(sketch, "E125", {"start": v(-8.56, -11.78) * mm, "end": v(8.56, 11.78) * mm, "construction": true});
            skLineSegment(sketch, "E126", {"start": v(-4.5, -13.85) * mm, "end": v(4.5, 13.85) * mm, "construction": true});
            skArc(sketch, "E127", {"start": v(11.78, 8.56) * mm, "mid": v(8.56, 11.78) * mm, "end": v(4.5, 13.85) * mm});
            skArc(sketch, "E128", {"start": v(11.78, -8.56) * mm, "mid": v(13.85, -4.5) * mm, "end": v(14.56, 0) * mm});
            skArc(sketch, "E129", {"start": v(-4.5, -13.85) * mm, "mid": v(0, -14.56) * mm, "end": v(4.5, -13.85) * mm});
            skArc(sketch, "E130", {"start": v(-14.56, 0) * mm, "mid": v(-13.85, -4.5) * mm, "end": v(-11.78, -8.56) * mm});
            skArc(sketch, "E131", {"start": v(-4.5, 13.85) * mm, "mid": v(-8.56, 11.78) * mm, "end": v(-11.78, 8.56) * mm});
            skArc(sketch, "E132", {"start": v(5.93, 8.16) * mm, "mid": v(3.12, 9.6) * mm, "end": v(0, 10.09) * mm});
            skArc(sketch, "E133", {"start": v(-5.93, 8.16) * mm, "mid": v(-8.16, 5.93) * mm, "end": v(-9.6, 3.12) * mm});
            skArc(sketch, "E134", {"start": v(-11.78, 8.56) * mm, "mid": v(-11.1, 5.67) * mm, "end": v(-9.6, 3.12) * mm});
            skArc(sketch, "E135", {"start": v(-4.5, 13.85) * mm, "mid": v(-5.64, 11.11) * mm, "end": v(-5.93, 8.16) * mm});
            skArc(sketch, "E136", {"start": v(4.5, 13.85) * mm, "mid": v(1.97, 12.3) * mm, "end": v(0, 10.09) * mm});
            skArc(sketch, "E137", {"start": v(11.78, 8.56) * mm, "mid": v(8.83, 8.8) * mm, "end": v(5.93, 8.16) * mm});
            skArc(sketch, "E138", {"start": v(-9.6, -3.12) * mm, "mid": v(-8.16, -5.93) * mm, "end": v(-5.93, -8.16) * mm});
            skArc(sketch, "E139", {"start": v(-14.56, 0) * mm, "mid": v(-12.31, -1.93) * mm, "end": v(-9.6, -3.12) * mm});
            skArc(sketch, "E140", {"start": v(-11.78, -8.56) * mm, "mid": v(-8.83, -8.8) * mm, "end": v(-5.93, -8.16) * mm});
            skArc(sketch, "E141", {"start": v(0, -10.09) * mm, "mid": v(3.12, -9.6) * mm, "end": v(5.93, -8.16) * mm});
            skArc(sketch, "E142", {"start": v(9.6, -3.12) * mm, "mid": v(10.09, 0) * mm, "end": v(9.6, 3.12) * mm});
            skArc(sketch, "E143", {"start": v(-4.5, -13.85) * mm, "mid": v(-1.97, -12.3) * mm, "end": v(0, -10.09) * mm});
            skArc(sketch, "E144", {"start": v(4.5, -13.85) * mm, "mid": v(5.64, -11.11) * mm, "end": v(5.93, -8.16) * mm});
            skArc(sketch, "E145", {"start": v(11.78, -8.56) * mm, "mid": v(11.1, -5.67) * mm, "end": v(9.6, -3.12) * mm});
            skArc(sketch, "E146", {"start": v(14.56, 0) * mm, "mid": v(12.31, 1.93) * mm, "end": v(9.6, 3.12) * mm});
            skSolve(sketch);
        }
        {
            var Q0;
            Q0=qSketchRegion(id+"F36",true);
            extrude(context, id + "F37", {"entities" : qUnion([Q0]), "operationType" : NewBodyOperationType.REMOVE, "oppositeDirection" : true, "depth" : 1.85 * mm});
        }
    });
